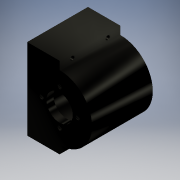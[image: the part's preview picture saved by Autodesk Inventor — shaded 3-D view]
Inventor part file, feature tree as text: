
AUTODESK INVENTOR PART (.ipt)
format: ipt  version: 2018 (Build 220112000, 112)  size: 161,792 bytes
history: native  units: mm
features: sketch x6, hole x5, other x1, extrude x1
ambient origin geometry x8: Origin, YZ Plane, XZ Plane, XY Plane, X Axis, Y Axis, Z Axis, Center Point
bodies: Body1 (feature_tree)
feature tree (13):
  other  "Sólido1"
  extrude  "Extrusión1"  Depth=64.0mm
  hole  "Agujero1"  [1 undecoded]
  hole  "Agujero2"  [1 undecoded]
  hole  "Agujero3"  [1 undecoded]
  hole  "Agujero4"  [1 undecoded]
  hole  "Agujero5"  [1 undecoded]
  sketch  "Boceto1"  dims[d0=52.0mm d1=64.0mm]
  sketch  "Boceto2"  dims[d2=40.0mm d3=80.0mm]
  sketch  "Boceto3"  dims[d4=32.0mm d5=32.0mm]
  sketch  "Boceto4"  dims[d6=67.0mm d7=0.0mm d8=52.0mm]
  sketch  "Boceto5"  dims[d9=52.0mm d10=6.0mm d11=4.0mm d12=2.0mm d13=90.0deg d14=60.0mm d15=0.0mm d16=26.0mm]
  sketch  "Boceto6"  dims[d17=26.0mm d18=6.0mm d19=4.0mm d20=2.0mm d21=90.0deg d22=60.0mm d23=0.0mm d24=35.5mm d25=4.0mm d26=4.0mm d27=4.0mm d28=4.0mm d29=4.0mm d30=6.0mm d31=4.0mm d32=2.0mm d33=90.0deg d34=60.0mm d35=0.0mm d36=200.0mm d37=6.0mm d38=4.0mm d39=2.0mm d40=90.0deg d41=7.0mm d42=0.0mm d43=35.0mm d44=40.0mm d45=30.0mm d46=72.0mm d47=4.0mm d48=4.0mm d49=4.0mm d50=4.0mm d51=4.0mm d52=6.0mm d53=4.0mm d54=2.0mm d55=90.0deg d56=32.0mm d57=0.0mm]
note: 5 required parameter values undecoded (feature->parameter linkage not recoverable at this tier; creation-order binding heuristic only, values carry confidence <= 0.55)
